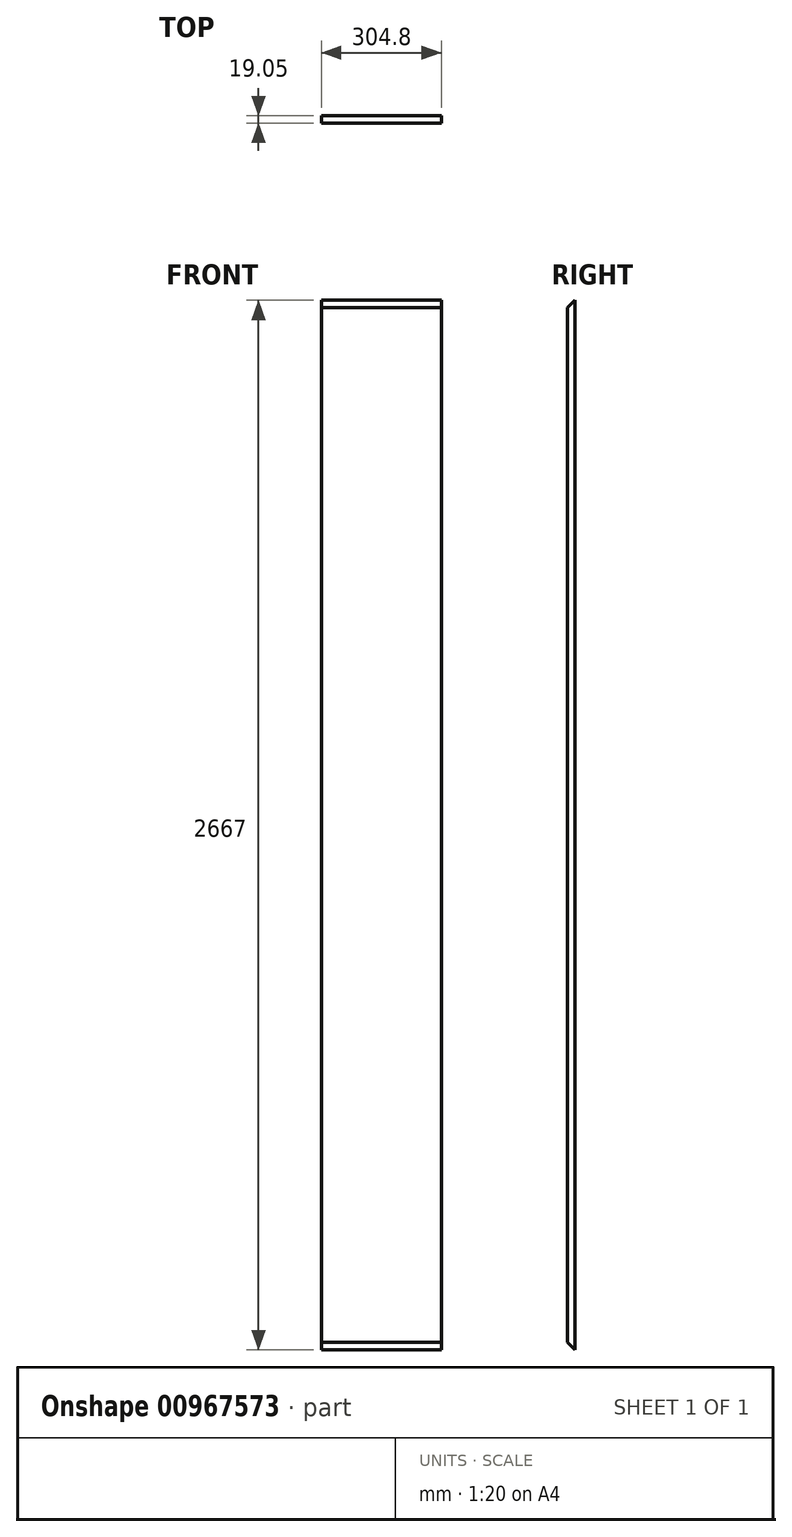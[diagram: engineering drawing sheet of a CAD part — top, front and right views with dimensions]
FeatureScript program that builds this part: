
annotation { "Feature Type Name" : "Feature", "Feature Type Description" : "" }
export const myFeature = defineFeature(function(context is Context, id is Id, definition is map)
    precondition{}
    {
        {
            var Q0;
            Q0=qCreatedBy(makeId("Front.planeOp"),FACE);
            var sketch = newSketch(context, id + "F0", { "sketchPlane" : qUnion([Q0])});
            skLineSegment(sketch, "E0.bottom", {"start": v(-18.3, 2623.49) * mm, "end": v(286.5, 2623.49) * mm});
            skLineSegment(sketch, "E0.top", {"start": v(-18.3, -43.51) * mm, "end": v(286.5, -43.51) * mm});
            skLineSegment(sketch, "E0.left", {"start": v(-18.3, 2623.49) * mm, "end": v(-18.3, -43.51) * mm});
            skLineSegment(sketch, "E0.right", {"start": v(286.5, 2623.49) * mm, "end": v(286.5, -43.51) * mm});
            skSolve(sketch);
        }
        {
            var Q0;
            Q0=makeQuery(id+"F0.imprint","IMPRINT",FACE,{"disambiguationData":[TD([[makeQuery(id+"F0.imprint","IMPRINT",EDGE,{"derivedFrom":sQuery(id+"F0.wireOp",EDGE,"E0.bottom")}),-1.0]])]});
            extrude(context, id + "F1", {"entities" : qUnion([Q0]), "depth" : 19.05 * mm, "offsetDistance" : 25.4 * mm});
        }
        {
            var Q0;
            Q0=makeQuery(id+"F1.opExtrude","CAP_EDGE",EDGE,{"disambiguationData":[OSD([sQuery(id+"F0.wireOp",EDGE,"E0.bottom")])],"isStart":false});
            var Q1;
            Q1=makeQuery(id+"F1.opExtrude","CAP_EDGE",EDGE,{"disambiguationData":[OSD([sQuery(id+"F0.wireOp",EDGE,"E0.top")])],"isStart":false});
            chamfer(context, id + "F2", {"entities" : qUnion([Q0, Q1]), "width" : 19.05 * mm, "tangentPropagation" : true});
        }
    });
